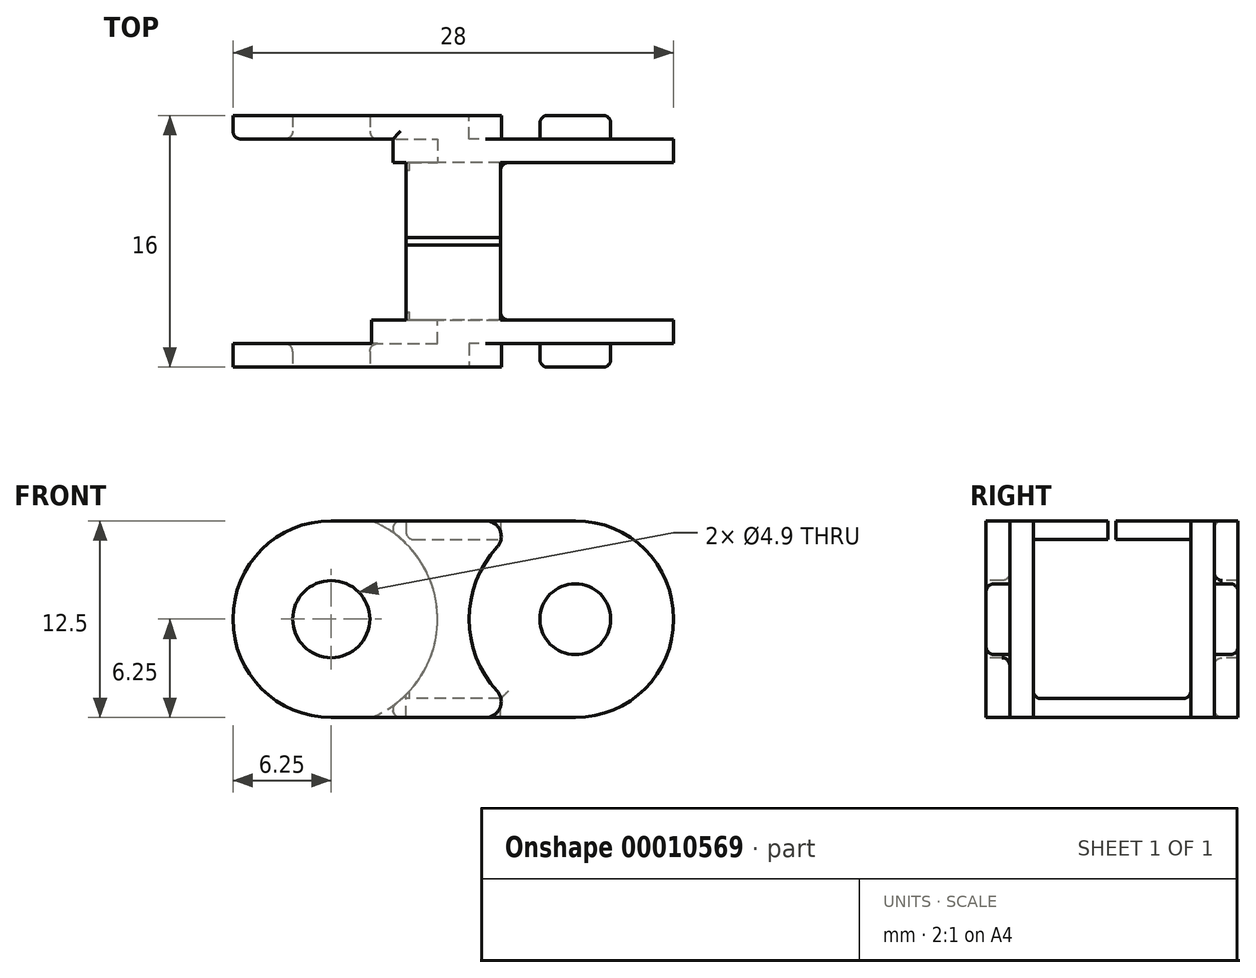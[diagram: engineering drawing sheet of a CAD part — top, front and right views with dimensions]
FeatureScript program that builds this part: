
annotation { "Feature Type Name" : "Feature", "Feature Type Description" : "" }
export const myFeature = defineFeature(function(context is Context, id is Id, definition is map)
    precondition{}
    {
        {
            var Q0;
            Q0=qCreatedBy(makeId("Top.planeOp"),FACE);
            var sketch = newSketch(context, id + "F0", { "sketchPlane" : qUnion([Q0])});
            skLineSegment(sketch, "E0.rect.bottom", {"start": v(14, -8) * mm, "end": v(-14, -8) * mm});
            skLineSegment(sketch, "E0.rect.top", {"start": v(14, 8) * mm, "end": v(-14, 8) * mm});
            skLineSegment(sketch, "E0.rect.left", {"start": v(14, -8) * mm, "end": v(14, 8) * mm});
            skLineSegment(sketch, "E0.rect.right", {"start": v(-14, -8) * mm, "end": v(-14, 8) * mm});
            skPoint(sketch, "E0.rect.middle", {"position": v(0, 0) * mm});
            skSolve(sketch);
        }
        {
            var Q0;
            Q0 = qSketchRegion(id + "F0", true);
            extrude(context, id + "F1", {"entities" : qUnion([Q0]), "depth" : 12.5 * mm, "symmetric" : true});
        }
        {
            var Q0;
            Q0=makeQuery(id+"F1.opExtrude","CAP_EDGE",EDGE,{"disambiguationData":[OSD([sQuery(id+"F0.wireOp",EDGE,"E0.rect.right")])],"isStart":false});
            var Q1;
            Q1=makeQuery(id+"F1.opExtrude","CAP_EDGE",EDGE,{"disambiguationData":[OSD([sQuery(id+"F0.wireOp",EDGE,"E0.rect.right")])],"isStart":true});
            var Q2;
            Q2=makeQuery(id+"F1.opExtrude","CAP_EDGE",EDGE,{"disambiguationData":[OSD([sQuery(id+"F0.wireOp",EDGE,"E0.rect.left")])],"isStart":false});
            var Q3;
            Q3=makeQuery(id+"F1.opExtrude","CAP_EDGE",EDGE,{"disambiguationData":[OSD([sQuery(id+"F0.wireOp",EDGE,"E0.rect.left")])],"isStart":true});
            fillet(context, id + "F2", {"entities" : qUnion([Q0, Q1, Q2, Q3]), "radius" : 6.25 * mm, "tangentPropagation" : true, "allowEdgeOverflow" : false});
        }
        {
            var Q0;
            Q0=makeQuery(id+"F1.opExtrude","CAP_FACE",FACE,{"disambiguationData":[OSD([sQuery(id+"F0.wireOp",EDGE,"E0.rect.bottom"),sQuery(id+"F0.wireOp",EDGE,"E0.rect.top"),sQuery(id+"F0.wireOp",EDGE,"E0.rect.left"),sQuery(id+"F0.wireOp",EDGE,"E0.rect.right")])],"isStart":false});
            var Q1;
            {var subQ0=sQuery(id+"F0.wireOp",EDGE,"E0.rect.right");Q1=makeQuery(id+"F2.opFillet","BLEND_FACE",FACE,{"disambiguationData":[OSD([subQ0]),TDD([makeQuery(id+"F1.opExtrude","CAP_EDGE",EDGE,{"disambiguationData":[OSD([subQ0])],"isStart":false})])]});}
            var Q2;
            Q2=makeQuery(id+"F1.opExtrude","SWEPT_FACE",FACE,{"disambiguationData":[OSD([sQuery(id+"F0.wireOp",EDGE,"E0.rect.right")])]});
            var Q3;
            {var subQ0=sQuery(id+"F0.wireOp",EDGE,"E0.rect.right");Q3=makeQuery(id+"F2.opFillet","BLEND_FACE",FACE,{"disambiguationData":[OSD([subQ0]),TDD([makeQuery(id+"F1.opExtrude","CAP_EDGE",EDGE,{"disambiguationData":[OSD([subQ0])],"isStart":true})])]});}
            var Q4;
            {var subQ0=sQuery(id+"F0.wireOp",EDGE,"E0.rect.left");Q4=makeQuery(id+"F2.opFillet","BLEND_FACE",FACE,{"disambiguationData":[OSD([subQ0]),TDD([makeQuery(id+"F1.opExtrude","CAP_EDGE",EDGE,{"disambiguationData":[OSD([subQ0])],"isStart":false})])]});}
            var Q5;
            Q5=makeQuery(id+"F1.opExtrude","SWEPT_FACE",FACE,{"disambiguationData":[OSD([sQuery(id+"F0.wireOp",EDGE,"E0.rect.left")])]});
            var Q6;
            {var subQ0=sQuery(id+"F0.wireOp",EDGE,"E0.rect.left");Q6=makeQuery(id+"F2.opFillet","BLEND_FACE",FACE,{"disambiguationData":[OSD([subQ0]),TDD([makeQuery(id+"F1.opExtrude","CAP_EDGE",EDGE,{"disambiguationData":[OSD([subQ0])],"isStart":true})])]});}
            shell(context, id + "F3", {"entities" : qUnion([Q0, Q1, Q2, Q3, Q4, Q5, Q6]), "thickness" : 3 * mm});
        }
        {
            var Q0;
            {var subQ0=sQuery(id+"F0.wireOp",EDGE,"E0.rect.bottom");var subQ1=sQuery(id+"F0.wireOp",EDGE,"E0.rect.top");var subQ2=sQuery(id+"F0.wireOp",EDGE,"E0.rect.left");var subQ3=sQuery(id+"F0.wireOp",EDGE,"E0.rect.right");Q0=makeQuery(id+"F3.opShell","OFFSET_FACE",FACE,{"disambiguationData":[OSD([subQ0,subQ1,subQ2,subQ3]),TDD([makeQuery(id+"F1.opExtrude","CAP_FACE",FACE,{"disambiguationData":[OSD([subQ0,subQ1,subQ2,subQ3])],"isStart":true})])]});}
            var sketch = newSketch(context, id + "F4", { "sketchPlane" : qUnion([Q0])});
            skLineSegment(sketch, "E1.bottom", {"start": v(-7.75, -5) * mm, "end": v(-3, -5) * mm});
            skLineSegment(sketch, "E1.top", {"start": v(-7.75, 5) * mm, "end": v(-3, 5) * mm});
            skLineSegment(sketch, "E1.left", {"start": v(-7.75, -5) * mm, "end": v(-7.75, 5) * mm});
            skLineSegment(sketch, "E1.right", {"start": v(-3, -5) * mm, "end": v(-3, 5) * mm});
            skLineSegment(sketch, "E2.bottom", {"start": v(7.75, -5) * mm, "end": v(3, -5) * mm});
            skLineSegment(sketch, "E2.top", {"start": v(7.75, 5) * mm, "end": v(3, 5) * mm});
            skLineSegment(sketch, "E2.left", {"start": v(7.75, -5) * mm, "end": v(7.75, 5) * mm});
            skLineSegment(sketch, "E2.right", {"start": v(3, -5) * mm, "end": v(3, 5) * mm});
            skSolve(sketch);
        }
        {
            var Q0;
            Q0 = qSketchRegion(id + "F4", true);
            extrude(context, id + "F5", {"entities" : qUnion([Q0]), "operationType" : NewBodyOperationType.REMOVE, "oppositeDirection" : true, "depth" : 25 * mm});
        }
        {
            var Q0;
            Q0=makeQuery(id+"F5.boolean.opBoolean","COPY",FACE,{"derivedFrom":makeQuery(id+"F5.opExtrude","SWEPT_FACE",FACE,{"disambiguationData":[OSD([sQuery(id+"F4.wireOp",EDGE,"E1.right")])]})});
            var sketch = newSketch(context, id + "F6", { "sketchPlane" : qUnion([Q0])});
            skLineSegment(sketch, "E3.bottom", {"start": v(-5, -3.25) * mm, "end": v(5, -3.25) * mm});
            skLineSegment(sketch, "E3.top", {"start": v(-5, -5.05) * mm, "end": v(5, -5.05) * mm});
            skLineSegment(sketch, "E3.left", {"start": v(-5, -3.25) * mm, "end": v(-5, -5.05) * mm});
            skLineSegment(sketch, "E3.right", {"start": v(5, -3.25) * mm, "end": v(5, -5.05) * mm});
            skSolve(sketch);
        }
        {
            var Q0;
            Q0 = qSketchRegion(id + "F6", true);
            extrude(context, id + "F7", {"entities" : qUnion([Q0]), "operationType" : NewBodyOperationType.REMOVE, "oppositeDirection" : true, "depth" : 25 * mm});
        }
        {
            var Q0;
            Q0=makeQuery(id+"F1.opExtrude","CAP_FACE",FACE,{"disambiguationData":[OSD([sQuery(id+"F0.wireOp",EDGE,"E0.rect.bottom"),sQuery(id+"F0.wireOp",EDGE,"E0.rect.top"),sQuery(id+"F0.wireOp",EDGE,"E0.rect.left"),sQuery(id+"F0.wireOp",EDGE,"E0.rect.right")])],"isStart":false});
            var sketch = newSketch(context, id + "F8", { "sketchPlane" : qUnion([Q0])});
            skLineSegment(sketch, "E4.bottom", {"start": v(-3, 5) * mm, "end": v(3, 5) * mm});
            skLineSegment(sketch, "E4.top", {"start": v(-3, -5) * mm, "end": v(3, -5) * mm});
            skLineSegment(sketch, "E4.left", {"start": v(-3, 5) * mm, "end": v(-3, -5) * mm});
            skLineSegment(sketch, "E4.right", {"start": v(3, 5) * mm, "end": v(3, -5) * mm});
            skSolve(sketch);
        }
        {
            var Q0;
            Q0 = qSketchRegion(id + "F8", true);
            extrude(context, id + "F9", {"entities" : qUnion([Q0]), "operationType" : NewBodyOperationType.ADD, "oppositeDirection" : true, "depth" : 1.2 * mm});
        }
        {
            var Q0;
            Q0=makeQuery(id+"F1.opExtrude","SWEPT_FACE",FACE,{"disambiguationData":[OSD([sQuery(id+"F0.wireOp",EDGE,"E0.rect.bottom")])]});
            var sketch = newSketch(context, id + "F10", { "sketchPlane" : qUnion([Q0])});
            skCircle(sketch, "E5", {"center": v(7.75, 0) * mm, "radius": 6.75 * mm});
            skSolve(sketch);
        }
        {
            var Q0;
            Q0 = qSketchRegion(id + "F10", true);
            extrude(context, id + "F11", {"entities" : qUnion([Q0]), "operationType" : NewBodyOperationType.REMOVE, "oppositeDirection" : true, "depth" : 1.5 * mm});
        }
        {
            var Q0;
            Q0=makeQuery(id+"F1.opExtrude","SWEPT_FACE",FACE,{"disambiguationData":[OSD([sQuery(id+"F0.wireOp",EDGE,"E0.rect.top")])]});
            var sketch = newSketch(context, id + "F12", { "sketchPlane" : qUnion([Q0])});
            skCircle(sketch, "E6", {"center": v(-7.75, 0) * mm, "radius": 6.75 * mm});
            skSolve(sketch);
        }
        {
            var Q0;
            Q0 = qSketchRegion(id + "F12", true);
            extrude(context, id + "F13", {"entities" : qUnion([Q0]), "operationType" : NewBodyOperationType.REMOVE, "oppositeDirection" : true, "depth" : 1.5 * mm});
        }
        {
            var Q0;
            {var subQ0=sQuery(id+"F0.wireOp",EDGE,"E0.rect.bottom");var subQ1=sQuery(id+"F0.wireOp",EDGE,"E0.rect.top");var subQ2=sQuery(id+"F0.wireOp",EDGE,"E0.rect.left");var subQ3=sQuery(id+"F0.wireOp",EDGE,"E0.rect.right");var subQ4=makeQuery(id+"F1.opExtrude","CAP_FACE",FACE,{"disambiguationData":[OSD([subQ0,subQ1,subQ2,subQ3])],"isStart":false});Q0=makeQuery(id+"F11.boolean.opBoolean","INTERSECT",EDGE,{"derivedFrom":[makeQuery(id+"FRDs2wFj56Co6Q4_1.boolean.opBoolean","MERGE",FACE,{"derivedFrom":[makeQuery(id+"F3.opShell","OFFSET_FACE",FACE,{"disambiguationData":[OSD([subQ0,subQ1,subQ2,subQ3]),TDD([subQ4])]}),subQ4,makeQuery(id+"FRDs2wFj56Co6Q4_1.opExtrude","CAP_FACE",FACE,{"disambiguationData":[OSD([sQuery(id+"F8wkNr267Ss34zO_1.wireOp",EDGE,"6609082b-c965-4ff1-a180-b40e3fbcedff.bottom"),sQuery(id+"F8wkNr267Ss34zO_1.wireOp",EDGE,"6609082b-c965-4ff1-a180-b40e3fbcedff.top"),sQuery(id+"F8wkNr267Ss34zO_1.wireOp",EDGE,"6609082b-c965-4ff1-a180-b40e3fbcedff.left"),sQuery(id+"F8wkNr267Ss34zO_1.wireOp",EDGE,"6609082b-c965-4ff1-a180-b40e3fbcedff.right")])],"isStart":true})]}),makeQuery(id+"F11.opExtrude","SWEPT_FACE",FACE,{"disambiguationData":[OSD([sQuery(id+"F10.wireOp",EDGE,"E5")])]})]});}
            var Q1;
            Q1=makeQuery(id+"F11.boolean.opBoolean","INTERSECT",EDGE,{"derivedFrom":[makeQuery(id+"F1.opExtrude","CAP_FACE",FACE,{"disambiguationData":[OSD([sQuery(id+"F0.wireOp",EDGE,"E0.rect.bottom"),sQuery(id+"F0.wireOp",EDGE,"E0.rect.top"),sQuery(id+"F0.wireOp",EDGE,"E0.rect.left"),sQuery(id+"F0.wireOp",EDGE,"E0.rect.right")])],"isStart":true}),makeQuery(id+"F11.opExtrude","SWEPT_FACE",FACE,{"disambiguationData":[OSD([sQuery(id+"F10.wireOp",EDGE,"E5")])]})]});
            var Q2;
            {var subQ0=sQuery(id+"F0.wireOp",EDGE,"E0.rect.bottom");var subQ1=sQuery(id+"F0.wireOp",EDGE,"E0.rect.top");var subQ2=sQuery(id+"F0.wireOp",EDGE,"E0.rect.left");var subQ3=sQuery(id+"F0.wireOp",EDGE,"E0.rect.right");var subQ4=makeQuery(id+"F1.opExtrude","CAP_FACE",FACE,{"disambiguationData":[OSD([subQ0,subQ1,subQ2,subQ3])],"isStart":false});Q2=makeQuery(id+"F13.boolean.opBoolean","INTERSECT",EDGE,{"derivedFrom":[makeQuery(id+"FRDs2wFj56Co6Q4_1.boolean.opBoolean","MERGE",FACE,{"derivedFrom":[makeQuery(id+"F3.opShell","OFFSET_FACE",FACE,{"disambiguationData":[OSD([subQ0,subQ1,subQ2,subQ3]),TDD([subQ4])]}),subQ4,makeQuery(id+"FRDs2wFj56Co6Q4_1.opExtrude","CAP_FACE",FACE,{"disambiguationData":[OSD([sQuery(id+"F8wkNr267Ss34zO_1.wireOp",EDGE,"6609082b-c965-4ff1-a180-b40e3fbcedff.bottom"),sQuery(id+"F8wkNr267Ss34zO_1.wireOp",EDGE,"6609082b-c965-4ff1-a180-b40e3fbcedff.top"),sQuery(id+"F8wkNr267Ss34zO_1.wireOp",EDGE,"6609082b-c965-4ff1-a180-b40e3fbcedff.left"),sQuery(id+"F8wkNr267Ss34zO_1.wireOp",EDGE,"6609082b-c965-4ff1-a180-b40e3fbcedff.right")])],"isStart":true})]}),makeQuery(id+"F13.opExtrude","SWEPT_FACE",FACE,{"disambiguationData":[OSD([sQuery(id+"F12.wireOp",EDGE,"E6")])]})]});}
            var Q3;
            Q3=makeQuery(id+"F13.boolean.opBoolean","INTERSECT",EDGE,{"derivedFrom":[makeQuery(id+"F1.opExtrude","CAP_FACE",FACE,{"disambiguationData":[OSD([sQuery(id+"F0.wireOp",EDGE,"E0.rect.bottom"),sQuery(id+"F0.wireOp",EDGE,"E0.rect.top"),sQuery(id+"F0.wireOp",EDGE,"E0.rect.left"),sQuery(id+"F0.wireOp",EDGE,"E0.rect.right")])],"isStart":true}),makeQuery(id+"F13.opExtrude","SWEPT_FACE",FACE,{"disambiguationData":[OSD([sQuery(id+"F12.wireOp",EDGE,"E6")])]})]});
            var Q4;
            {var subQ0=sQuery(id+"F0.wireOp",EDGE,"E0.rect.left");var subQ1=sQuery(id+"F0.wireOp",EDGE,"E0.rect.bottom");var subQ2=sQuery(id+"F0.wireOp",EDGE,"E0.rect.top");var subQ3=sQuery(id+"F0.wireOp",EDGE,"E0.rect.right");var subQ4=makeQuery(id+"F1.opExtrude","CAP_FACE",FACE,{"disambiguationData":[OSD([subQ1,subQ2,subQ0,subQ3])],"isStart":false});Q4=makeQuery(id+"F11.boolean.opBoolean","SPLIT",EDGE,{"disambiguationData":[TD([makeQuery(id+"F1.opExtrude","SWEPT_FACE",FACE,{"disambiguationData":[OSD([subQ1])]})])],"derivedFrom":makeQuery(id+"F2.opFillet","BLEND_EDGE",EDGE,{"blendedFrom":[makeQuery(id+"F1.opExtrude","CAP_EDGE",EDGE,{"disambiguationData":[OSD([subQ0])],"isStart":false}),subQ4],"blendedInto":[subQ4]})});}
            var Q5;
            {var subQ0=sQuery(id+"F0.wireOp",EDGE,"E0.rect.bottom");var subQ1=sQuery(id+"F0.wireOp",EDGE,"E0.rect.top");var subQ2=sQuery(id+"F0.wireOp",EDGE,"E0.rect.left");var subQ3=sQuery(id+"F0.wireOp",EDGE,"E0.rect.right");var subQ4=makeQuery(id+"F1.opExtrude","CAP_FACE",FACE,{"disambiguationData":[OSD([subQ0,subQ1,subQ2,subQ3])],"isStart":true});Q5=makeQuery(id+"F11.boolean.opBoolean","SPLIT",EDGE,{"disambiguationData":[TD([makeQuery(id+"F1.opExtrude","SWEPT_FACE",FACE,{"disambiguationData":[OSD([subQ0])]})])],"derivedFrom":makeQuery(id+"F3.opShell","OFFSET_EDGE",EDGE,{"disambiguationData":[OSD([subQ0,subQ1,subQ2,subQ3]),TDD([makeQuery(id+"F2.opFillet","BLEND_EDGE",EDGE,{"blendedFrom":[makeQuery(id+"F1.opExtrude","CAP_EDGE",EDGE,{"disambiguationData":[OSD([subQ2])],"isStart":true}),subQ4],"blendedInto":[subQ4]})]),OD(0.0)]})});}
            var Q6;
            {var subQ0=sQuery(id+"F0.wireOp",EDGE,"E0.rect.bottom");var subQ1=sQuery(id+"F0.wireOp",EDGE,"E0.rect.top");var subQ2=sQuery(id+"F0.wireOp",EDGE,"E0.rect.left");var subQ3=sQuery(id+"F0.wireOp",EDGE,"E0.rect.right");var subQ4=makeQuery(id+"F1.opExtrude","CAP_FACE",FACE,{"disambiguationData":[OSD([subQ0,subQ1,subQ2,subQ3])],"isStart":false});Q6=makeQuery(id+"F13.boolean.opBoolean","SPLIT",EDGE,{"disambiguationData":[TD([makeQuery(id+"F1.opExtrude","SWEPT_FACE",FACE,{"disambiguationData":[OSD([subQ1])]})])],"derivedFrom":makeQuery(id+"F3.opShell","OFFSET_EDGE",EDGE,{"disambiguationData":[OSD([subQ0,subQ1,subQ2,subQ3]),TDD([makeQuery(id+"F2.opFillet","BLEND_EDGE",EDGE,{"blendedFrom":[makeQuery(id+"F1.opExtrude","CAP_EDGE",EDGE,{"disambiguationData":[OSD([subQ2])],"isStart":false}),subQ4],"blendedInto":[subQ4]})])]})});}
            var Q7;
            {var subQ0=sQuery(id+"F0.wireOp",EDGE,"E0.rect.left");var subQ1=sQuery(id+"F0.wireOp",EDGE,"E0.rect.top");var subQ2=makeQuery(id+"F1.opExtrude","CAP_FACE",FACE,{"disambiguationData":[OSD([sQuery(id+"F0.wireOp",EDGE,"E0.rect.bottom"),subQ1,subQ0,sQuery(id+"F0.wireOp",EDGE,"E0.rect.right")])],"isStart":true});Q7=makeQuery(id+"F13.boolean.opBoolean","SPLIT",EDGE,{"disambiguationData":[TD([makeQuery(id+"F1.opExtrude","SWEPT_FACE",FACE,{"disambiguationData":[OSD([subQ1])]})])],"derivedFrom":makeQuery(id+"F2.opFillet","BLEND_EDGE",EDGE,{"blendedFrom":[makeQuery(id+"F1.opExtrude","CAP_EDGE",EDGE,{"disambiguationData":[OSD([subQ0])],"isStart":true}),subQ2],"blendedInto":[subQ2]})});}
            fillet(context, id + "F14", {"entities" : qUnion([Q0, Q1, Q2, Q3, Q4, Q5, Q6, Q7]), "radius" : 1 * mm, "tangentPropagation" : true, "allowEdgeOverflow" : false});
        }
        {
            var Q0;
            Q0=makeQuery(id+"F11.boolean.opBoolean","COPY",FACE,{"derivedFrom":makeQuery(id+"F11.opExtrude","CAP_FACE",FACE,{"disambiguationData":[OSD([sQuery(id+"F10.wireOp",EDGE,"E5")])],"isStart":false})});
            var sketch = newSketch(context, id + "F15", { "sketchPlane" : qUnion([Q0])});
            skCircle(sketch, "E7", {"center": v(7.75, 0) * mm, "radius": 2.25 * mm});
            skSolve(sketch);
        }
        {
            var Q0;
            Q0 = qSketchRegion(id + "F15", true);
            extrude(context, id + "F16", {"entities" : qUnion([Q0]), "operationType" : NewBodyOperationType.ADD, "depth" : 1.5 * mm});
        }
        {
            var Q0;
            Q0=makeQuery(id+"F13.boolean.opBoolean","COPY",FACE,{"derivedFrom":makeQuery(id+"F13.opExtrude","CAP_FACE",FACE,{"disambiguationData":[OSD([sQuery(id+"F12.wireOp",EDGE,"E6")])],"isStart":false})});
            var sketch = newSketch(context, id + "F17", { "sketchPlane" : qUnion([Q0])});
            skCircle(sketch, "E8", {"center": v(-7.75, 0) * mm, "radius": 2.25 * mm});
            skSolve(sketch);
        }
        {
            var Q0;
            Q0 = qSketchRegion(id + "F17", true);
            extrude(context, id + "F18", {"entities" : qUnion([Q0]), "operationType" : NewBodyOperationType.ADD, "depth" : 1.5 * mm});
        }
        {
            var Q0;
            Q0=makeQuery(id+"F1.opExtrude","SWEPT_FACE",FACE,{"disambiguationData":[OSD([sQuery(id+"F0.wireOp",EDGE,"E0.rect.bottom")])]});
            var sketch = newSketch(context, id + "F19", { "sketchPlane" : qUnion([Q0])});
            skCircle(sketch, "E9", {"center": v(-7.75, 0) * mm, "radius": 2.45 * mm});
            skSolve(sketch);
        }
        {
            var Q0;
            Q0 = qSketchRegion(id + "F19", true);
            extrude(context, id + "F20", {"entities" : qUnion([Q0]), "operationType" : NewBodyOperationType.REMOVE, "endBound" : BoundingType.THROUGH_ALL, "oppositeDirection" : true, "depth" : 25 * mm});
        }
        {
            var Q0;
            Q0=makeQuery(id+"FHNYXm6BuEGCrrz_1.boolean.opBoolean","MERGE",FACE,{"derivedFrom":[makeQuery(id+"F3.opShell","OFFSET_FACE",FACE,{"disambiguationData":[OSD([sQuery(id+"F0.wireOp",EDGE,"E0.rect.top")])]}),makeQuery(id+"FHNYXm6BuEGCrrz_1.opExtrude","SWEPT_FACE",FACE,{"disambiguationData":[OSD([sQuery(id+"FrscQX9RS2ccQFD_1.wireOp",EDGE,"376541ee-2e4d-4804-9836-3ca692176c24.right")])]})]});
            var sketch = newSketch(context, id + "F21", { "sketchPlane" : qUnion([Q0])});
            skCircle(sketch, "E10", {"center": v(-7.75, 0) * mm, "radius": 6.75 * mm});
            skSolve(sketch);
        }
        {
            var Q0;
            Q0 = qSketchRegion(id + "F21", true);
            extrude(context, id + "F22", {"entities" : qUnion([Q0]), "operationType" : NewBodyOperationType.REMOVE, "oppositeDirection" : true, "depth" : 1.5 * mm});
        }
        {
            var Q0;
            Q0=makeQuery(id+"FHNYXm6BuEGCrrz_1.boolean.opBoolean","MERGE",FACE,{"derivedFrom":[makeQuery(id+"F3.opShell","OFFSET_FACE",FACE,{"disambiguationData":[OSD([sQuery(id+"F0.wireOp",EDGE,"E0.rect.bottom")])]}),makeQuery(id+"FHNYXm6BuEGCrrz_1.opExtrude","SWEPT_FACE",FACE,{"disambiguationData":[OSD([sQuery(id+"FrscQX9RS2ccQFD_1.wireOp",EDGE,"376541ee-2e4d-4804-9836-3ca692176c24.left")])]})]});
            var sketch = newSketch(context, id + "F23", { "sketchPlane" : qUnion([Q0])});
            skCircle(sketch, "E11", {"center": v(7.75, 0) * mm, "radius": 6.75 * mm});
            skSolve(sketch);
        }
        {
            var Q0;
            Q0 = qSketchRegion(id + "F23", true);
            extrude(context, id + "F24", {"entities" : qUnion([Q0]), "operationType" : NewBodyOperationType.REMOVE, "oppositeDirection" : true, "depth" : 1.5 * mm});
        }
        {
            var Q0;
            {var subQ0=sQuery(id+"F0.wireOp",EDGE,"E0.rect.bottom");var subQ1=sQuery(id+"F0.wireOp",EDGE,"E0.rect.top");var subQ2=sQuery(id+"F0.wireOp",EDGE,"E0.rect.left");var subQ3=sQuery(id+"F0.wireOp",EDGE,"E0.rect.right");var subQ4=makeQuery(id+"F1.opExtrude","CAP_FACE",FACE,{"disambiguationData":[OSD([subQ0,subQ1,subQ2,subQ3])],"isStart":false});Q0=makeQuery(id+"F22.boolean.opBoolean","INTERSECT",EDGE,{"derivedFrom":[makeQuery(id+"FRDs2wFj56Co6Q4_1.boolean.opBoolean","MERGE",FACE,{"derivedFrom":[makeQuery(id+"F3.opShell","OFFSET_FACE",FACE,{"disambiguationData":[OSD([subQ0,subQ1,subQ2,subQ3]),TDD([subQ4])]}),subQ4,makeQuery(id+"FRDs2wFj56Co6Q4_1.opExtrude","CAP_FACE",FACE,{"disambiguationData":[OSD([sQuery(id+"F8wkNr267Ss34zO_1.wireOp",EDGE,"6609082b-c965-4ff1-a180-b40e3fbcedff.bottom"),sQuery(id+"F8wkNr267Ss34zO_1.wireOp",EDGE,"6609082b-c965-4ff1-a180-b40e3fbcedff.top"),sQuery(id+"F8wkNr267Ss34zO_1.wireOp",EDGE,"6609082b-c965-4ff1-a180-b40e3fbcedff.left"),sQuery(id+"F8wkNr267Ss34zO_1.wireOp",EDGE,"6609082b-c965-4ff1-a180-b40e3fbcedff.right")])],"isStart":true})]}),makeQuery(id+"F22.opExtrude","SWEPT_FACE",FACE,{"disambiguationData":[OSD([sQuery(id+"F21.wireOp",EDGE,"E10")])]})]});}
            var Q1;
            Q1=makeQuery(id+"F22.boolean.opBoolean","INTERSECT",EDGE,{"derivedFrom":[makeQuery(id+"F1.opExtrude","CAP_FACE",FACE,{"disambiguationData":[OSD([sQuery(id+"F0.wireOp",EDGE,"E0.rect.bottom"),sQuery(id+"F0.wireOp",EDGE,"E0.rect.top"),sQuery(id+"F0.wireOp",EDGE,"E0.rect.left"),sQuery(id+"F0.wireOp",EDGE,"E0.rect.right")])],"isStart":true}),makeQuery(id+"F22.opExtrude","SWEPT_FACE",FACE,{"disambiguationData":[OSD([sQuery(id+"F21.wireOp",EDGE,"E10")])]})]});
            var Q2;
            {var subQ0=sQuery(id+"F0.wireOp",EDGE,"E0.rect.bottom");var subQ1=sQuery(id+"F0.wireOp",EDGE,"E0.rect.top");var subQ2=sQuery(id+"F0.wireOp",EDGE,"E0.rect.left");var subQ3=sQuery(id+"F0.wireOp",EDGE,"E0.rect.right");var subQ4=makeQuery(id+"F1.opExtrude","CAP_FACE",FACE,{"disambiguationData":[OSD([subQ0,subQ1,subQ2,subQ3])],"isStart":false});Q2=makeQuery(id+"F22.boolean.opBoolean","INTERSECT",EDGE,{"derivedFrom":[makeQuery(id+"FRDs2wFj56Co6Q4_1.boolean.opBoolean","MERGE",FACE,{"derivedFrom":[makeQuery(id+"F3.opShell","OFFSET_FACE",FACE,{"disambiguationData":[OSD([subQ0,subQ1,subQ2,subQ3]),TDD([subQ4])]}),subQ4,makeQuery(id+"FRDs2wFj56Co6Q4_1.opExtrude","CAP_FACE",FACE,{"disambiguationData":[OSD([sQuery(id+"F8wkNr267Ss34zO_1.wireOp",EDGE,"6609082b-c965-4ff1-a180-b40e3fbcedff.bottom"),sQuery(id+"F8wkNr267Ss34zO_1.wireOp",EDGE,"6609082b-c965-4ff1-a180-b40e3fbcedff.top"),sQuery(id+"F8wkNr267Ss34zO_1.wireOp",EDGE,"6609082b-c965-4ff1-a180-b40e3fbcedff.left"),sQuery(id+"F8wkNr267Ss34zO_1.wireOp",EDGE,"6609082b-c965-4ff1-a180-b40e3fbcedff.right")])],"isStart":true})]}),makeQuery(id+"F22.opExtrude","CAP_FACE",FACE,{"disambiguationData":[OSD([sQuery(id+"F21.wireOp",EDGE,"E10")])],"isStart":false})]});}
            var Q3;
            Q3=makeQuery(id+"F22.boolean.opBoolean","INTERSECT",EDGE,{"derivedFrom":[makeQuery(id+"F3.opShell","OFFSET_FACE",FACE,{"disambiguationData":[OSD([sQuery(id+"F0.wireOp",EDGE,"E0.rect.right")])]}),makeQuery(id+"F22.opExtrude","CAP_FACE",FACE,{"disambiguationData":[OSD([sQuery(id+"F21.wireOp",EDGE,"E10")])],"isStart":false})]});
            fillet(context, id + "F25", {"entities" : qUnion([Q0, Q1, Q2, Q3]), "radius" : 0.5 * mm, "tangentPropagation" : true, "allowEdgeOverflow" : false});
        }
        {
            var Q0;
            Q0=makeQuery(id+"F7.boolean.opBoolean","COPY",EDGE,{"derivedFrom":makeQuery(id+"F7.opExtrude","CAP_EDGE",EDGE,{"disambiguationData":[OSD([sQuery(id+"F6.wireOp",EDGE,"E3.top")])],"isStart":true})});
            var Q1;
            Q1=makeQuery(id+"F9.opExtrude","CAP_EDGE",EDGE,{"disambiguationData":[OSD([sQuery(id+"F8.wireOp",EDGE,"E4.left")])],"isStart":false});
            fillet(context, id + "F26", {"entities" : qUnion([Q0, Q1]), "radius" : 0.5 * mm, "allowEdgeOverflow" : false});
        }
        {
            var Q0;
            {var subQ0=sQuery(id+"F0.wireOp",EDGE,"E0.rect.bottom");var subQ1=sQuery(id+"F4.wireOp",EDGE,"E1.bottom");var subQ2=sQuery(id+"F6.wireOp",EDGE,"E3.top");var subQ3=sQuery(id+"F6.wireOp",EDGE,"E3.right");Q0=makeQuery(id+"F24.boolean.opBoolean","SPLIT",EDGE,{"disambiguationData":[TD([makeQuery(id+"F5.boolean.opBoolean","COPY",FACE,{"derivedFrom":makeQuery(id+"F5.opExtrude","SWEPT_FACE",FACE,{"disambiguationData":[OSD([sQuery(id+"F4.wireOp",EDGE,"E2.right")])]})})])],"derivedFrom":makeQuery(id+"F7.boolean.opBoolean","COPY",EDGE,{"derivedFrom":makeQuery(id+"F7.opExtrude","SWEPT_EDGE",EDGE,{"disambiguationData":[OSD([subQ0,subQ1,sQuery(id+"F4.wireOp",EDGE,"E1.right"),subQ2,subQ3])]})})});}
            var Q1;
            {var subQ0=sQuery(id+"F8.wireOp",EDGE,"E4.top");var subQ2=sQuery(id+"F8.wireOp",EDGE,"E4.right");Q1=makeQuery(id+"F24.boolean.opBoolean","SPLIT",EDGE,{"disambiguationData":[TD([makeQuery(id+"F9.opExtrude","SWEPT_FACE",FACE,{"disambiguationData":[OSD([subQ2])]})])],"derivedFrom":makeQuery(id+"F9.opExtrude","CAP_EDGE",EDGE,{"disambiguationData":[OSD([subQ0])],"isStart":false})});}
            var Q2;
            {var subQ0=sQuery(id+"F0.wireOp",EDGE,"E0.rect.top");var subQ1=sQuery(id+"F4.wireOp",EDGE,"E1.top");var subQ2=sQuery(id+"F6.wireOp",EDGE,"E3.top");var subQ3=sQuery(id+"F6.wireOp",EDGE,"E3.left");Q2=makeQuery(id+"F22.boolean.opBoolean","SPLIT",EDGE,{"disambiguationData":[TD([makeQuery(id+"F5.boolean.opBoolean","COPY",FACE,{"derivedFrom":makeQuery(id+"F5.opExtrude","SWEPT_FACE",FACE,{"disambiguationData":[OSD([sQuery(id+"F4.wireOp",EDGE,"E2.right")])]})})])],"derivedFrom":makeQuery(id+"F7.boolean.opBoolean","COPY",EDGE,{"derivedFrom":makeQuery(id+"F7.opExtrude","SWEPT_EDGE",EDGE,{"disambiguationData":[OSD([subQ0,subQ1,sQuery(id+"F4.wireOp",EDGE,"E1.right"),subQ2,subQ3])]})})});}
            var Q3;
            {var subQ0=sQuery(id+"F8.wireOp",EDGE,"E4.bottom");var subQ2=sQuery(id+"F8.wireOp",EDGE,"E4.right");Q3=makeQuery(id+"F22.boolean.opBoolean","SPLIT",EDGE,{"disambiguationData":[TD([makeQuery(id+"F9.opExtrude","SWEPT_FACE",FACE,{"disambiguationData":[OSD([subQ2])]})])],"derivedFrom":makeQuery(id+"F9.opExtrude","CAP_EDGE",EDGE,{"disambiguationData":[OSD([subQ0])],"isStart":false})});}
            var Q4;
            Q4=makeQuery(id+"F9.opExtrude","SWEPT_EDGE",EDGE,{"disambiguationData":[OSD([sQuery(id+"F0.wireOp",EDGE,"E0.rect.top"),sQuery(id+"F8.wireOp",EDGE,"E4.bottom"),sQuery(id+"F8.wireOp",EDGE,"E4.right")])]});
            var Q5;
            Q5=makeQuery(id+"F9.opExtrude","SWEPT_EDGE",EDGE,{"disambiguationData":[OSD([sQuery(id+"F8.wireOp",EDGE,"E4.top"),sQuery(id+"F8.wireOp",EDGE,"E4.right")])]});
            var Q6;
            Q6=makeQuery(id+"F5.boolean.opBoolean","COPY",EDGE,{"derivedFrom":makeQuery(id+"F5.opExtrude","SWEPT_EDGE",EDGE,{"disambiguationData":[OSD([sQuery(id+"F0.wireOp",EDGE,"E0.rect.bottom"),sQuery(id+"F4.wireOp",EDGE,"E2.bottom"),sQuery(id+"F4.wireOp",EDGE,"E2.right")])]})});
            var Q7;
            Q7=makeQuery(id+"F5.boolean.opBoolean","COPY",EDGE,{"derivedFrom":makeQuery(id+"F5.opExtrude","SWEPT_EDGE",EDGE,{"disambiguationData":[OSD([sQuery(id+"F0.wireOp",EDGE,"E0.rect.top"),sQuery(id+"F4.wireOp",EDGE,"E2.top"),sQuery(id+"F4.wireOp",EDGE,"E2.right")])]})});
            fillet(context, id + "F27", {"entities" : qUnion([Q0, Q1, Q2, Q3, Q4, Q5, Q6, Q7]), "radius" : 0.5 * mm, "tangentPropagation" : true, "allowEdgeOverflow" : false});
        }
        {
            var Q0;
            Q0=makeQuery(id+"F16.opExtrude","CAP_EDGE",EDGE,{"disambiguationData":[OSD([sQuery(id+"F15.wireOp",EDGE,"E7")])],"isStart":false});
            var Q1;
            Q1=makeQuery(id+"F18.opExtrude","CAP_EDGE",EDGE,{"disambiguationData":[OSD([sQuery(id+"F17.wireOp",EDGE,"E8")])],"isStart":false});
            var Q2;
            Q2=makeQuery(id+"F22.boolean.opBoolean","INTERSECT",EDGE,{"derivedFrom":[makeQuery(id+"F20.boolean.opBoolean","COPY",FACE,{"disambiguationData":[OD(1.0)],"derivedFrom":makeQuery(id+"F20.opExtrude","SWEPT_FACE",FACE,{"disambiguationData":[OSD([sQuery(id+"F19.wireOp",EDGE,"E9")])]})}),makeQuery(id+"F22.opExtrude","CAP_FACE",FACE,{"disambiguationData":[OSD([sQuery(id+"F21.wireOp",EDGE,"E10")])],"isStart":false})]});
            var Q3;
            Q3=makeQuery(id+"F24.boolean.opBoolean","INTERSECT",EDGE,{"derivedFrom":[makeQuery(id+"F20.boolean.opBoolean","COPY",FACE,{"disambiguationData":[OD(0.0)],"derivedFrom":makeQuery(id+"F20.opExtrude","SWEPT_FACE",FACE,{"disambiguationData":[OSD([sQuery(id+"F19.wireOp",EDGE,"E9")])]})}),makeQuery(id+"F24.opExtrude","CAP_FACE",FACE,{"disambiguationData":[OSD([sQuery(id+"F23.wireOp",EDGE,"E11")])],"isStart":false})]});
            fillet(context, id + "F28", {"entities" : qUnion([Q0, Q1, Q2, Q3]), "radius" : 0.5 * mm, "tangentPropagation" : true, "allowEdgeOverflow" : false});
        }
        {
            var Q0;
            {var subQ0=sQuery(id+"F0.wireOp",EDGE,"E0.rect.bottom");var subQ1=sQuery(id+"F0.wireOp",EDGE,"E0.rect.top");var subQ2=sQuery(id+"F0.wireOp",EDGE,"E0.rect.left");var subQ3=sQuery(id+"F0.wireOp",EDGE,"E0.rect.right");var subQ4=makeQuery(id+"F1.opExtrude","CAP_FACE",FACE,{"disambiguationData":[OSD([subQ0,subQ1,subQ2,subQ3])],"isStart":false});Q0=makeQuery(id+"F9.boolean.opBoolean","MERGE",FACE,{"derivedFrom":[makeQuery(id+"F3.opShell","OFFSET_FACE",FACE,{"disambiguationData":[OSD([subQ0,subQ1,subQ2,subQ3]),TDD([subQ4])]}),subQ4,makeQuery(id+"F9.opExtrude","CAP_FACE",FACE,{"disambiguationData":[OSD([sQuery(id+"F8.wireOp",EDGE,"E4.bottom"),sQuery(id+"F8.wireOp",EDGE,"E4.top"),sQuery(id+"F8.wireOp",EDGE,"E4.left"),sQuery(id+"F8.wireOp",EDGE,"E4.right")])],"isStart":true})]});}
            var sketch = newSketch(context, id + "F29", { "sketchPlane" : qUnion([Q0])});
            skLineSegment(sketch, "E12.rect.bottom", {"start": v(5, -0.25) * mm, "end": v(-5, -0.25) * mm});
            skLineSegment(sketch, "E12.rect.top", {"start": v(5, 0.25) * mm, "end": v(-5, 0.25) * mm});
            skLineSegment(sketch, "E12.rect.left", {"start": v(5, -0.25) * mm, "end": v(5, 0.25) * mm});
            skLineSegment(sketch, "E12.rect.right", {"start": v(-5, -0.25) * mm, "end": v(-5, 0.25) * mm});
            skPoint(sketch, "E12.rect.middle", {"position": v(0, 0) * mm});
            skSolve(sketch);
        }
        {
            var Q0;
            Q0 = qSketchRegion(id + "F29", true);
            var Q1;
            Q1=makeQuery(id+"F9.opExtrude","CAP_FACE",FACE,{"disambiguationData":[OSD([sQuery(id+"F8.wireOp",EDGE,"E4.bottom"),sQuery(id+"F8.wireOp",EDGE,"E4.top"),sQuery(id+"F8.wireOp",EDGE,"E4.left"),sQuery(id+"F8.wireOp",EDGE,"E4.right")])],"isStart":false});
            extrude(context, id + "F30", {"entities" : qUnion([Q0]), "operationType" : NewBodyOperationType.REMOVE, "endBound" : BoundingType.UP_TO_SURFACE, "oppositeDirection" : true, "endBoundEntityFace" : qUnion([Q1]), "depth" : 25 * mm});
        }
    });
